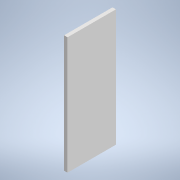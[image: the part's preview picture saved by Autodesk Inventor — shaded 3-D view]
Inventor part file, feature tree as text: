
AUTODESK INVENTOR PART (.ipt)
format: ipt  version: 2021 (Build 250183000, 183)  size: 88,576 bytes
history: native  units: in
note: dims shown in document units (in); Inventor stores cm internally (conversion verified against a paired STEP export)
features: extrude x1, sketch x1
ambient origin geometry x8: Origin, YZ Plane, XZ Plane, XY Plane, X Axis, Y Axis, Z Axis, Center Point
bodies: Solid1 (feature_tree)
feature tree (2):
  extrude  "Extrusion1"  [1 undecoded]
  sketch  "Sketch1"  dims[d1=7.0in d2=0.0in]
note: 1 required parameter value undecoded (feature->parameter linkage not recoverable at this tier; creation-order binding heuristic only, values carry confidence <= 0.55)
